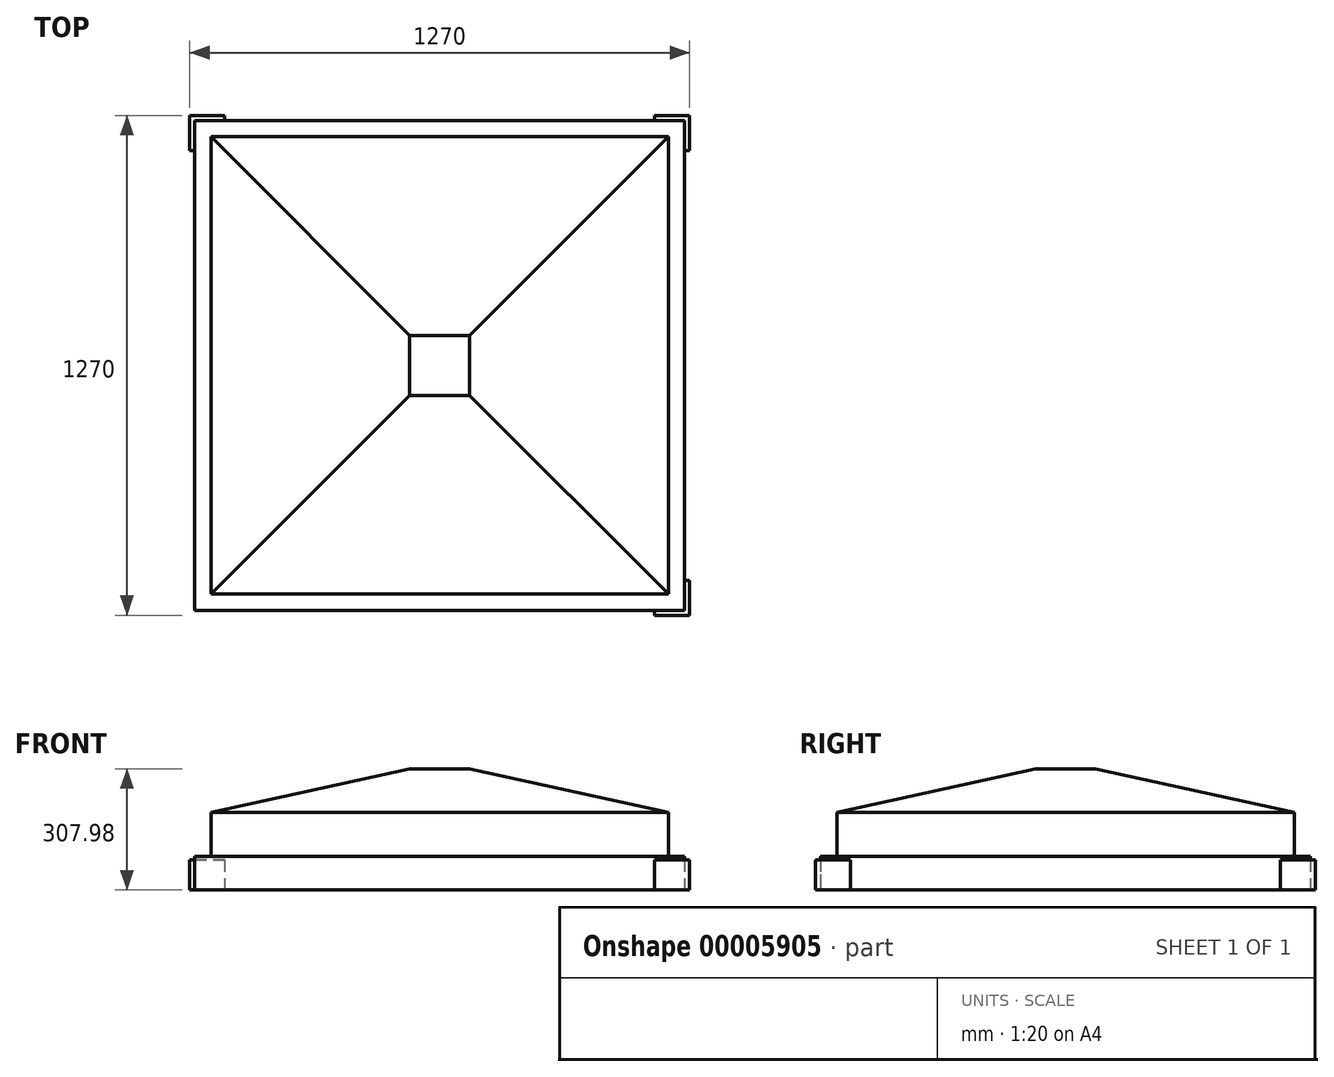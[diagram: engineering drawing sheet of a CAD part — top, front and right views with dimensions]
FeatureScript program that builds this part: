
annotation { "Feature Type Name" : "Feature", "Feature Type Description" : "" }
export const myFeature = defineFeature(function(context is Context, id is Id, definition is map)
    precondition{}
    {
        {
            var Q0;
            Q0=qCreatedBy(makeId("Top.planeOp"),FACE);
            var sketch = newSketch(context, id + "F0", { "sketchPlane" : qUnion([Q0])});
            skLineSegment(sketch, "E0.bottom", {"start": v(0, 0) * mm, "end": v(1244.6, 0) * mm});
            skLineSegment(sketch, "E0.top", {"start": v(0, 1244.6) * mm, "end": v(1244.6, 1244.6) * mm});
            skLineSegment(sketch, "E0.left", {"start": v(0, 0) * mm, "end": v(0, 1244.6) * mm});
            skLineSegment(sketch, "E0.right", {"start": v(1244.6, 0) * mm, "end": v(1244.6, 1244.6) * mm});
            skSolve(sketch);
        }
        {
            var Q0;
            Q0=makeQuery(id+"F0.imprint","IMPRINT",FACE,{"disambiguationData":[TD([[makeQuery(id+"F0.imprint","IMPRINT",EDGE,{"derivedFrom":sQuery(id+"F0.wireOp",EDGE,"E0.bottom")}),1.0]])]});
            extrude(context, id + "F1", {"entities" : qUnion([Q0]), "depth" : 85.72 * mm});
        }
        {
            var Q0;
            Q0=makeQuery(id+"F1.opExtrude","CAP_FACE",FACE,{"disambiguationData":[OSD([sQuery(id+"F0.wireOp",EDGE,"E0.bottom"),sQuery(id+"F0.wireOp",EDGE,"E0.top"),sQuery(id+"F0.wireOp",EDGE,"E0.left"),sQuery(id+"F0.wireOp",EDGE,"E0.right")])],"isStart":false});
            var sketch = newSketch(context, id + "F2", { "sketchPlane" : qUnion([Q0])});
            skLineSegment(sketch, "E1.bottom", {"start": v(41.28, 1203.33) * mm, "end": v(1203.33, 1203.33) * mm});
            skLineSegment(sketch, "E1.top", {"start": v(41.28, 41.28) * mm, "end": v(1203.33, 41.28) * mm});
            skLineSegment(sketch, "E1.left", {"start": v(41.27, 1203.33) * mm, "end": v(41.28, 41.28) * mm});
            skLineSegment(sketch, "E1.right", {"start": v(1203.33, 1203.33) * mm, "end": v(1203.33, 41.28) * mm});
            skLineSegment(sketch, "E2.0", {"start": v(0, 0) * mm, "end": v(0, 1244.6) * mm});
            skLineSegment(sketch, "E3.0", {"start": v(0, 1244.6) * mm, "end": v(1244.6, 1244.6) * mm});
            skLineSegment(sketch, "E4", {"start": v(0, 887.33) * mm, "end": v(41.28, 887.33) * mm, "construction": true});
            skLineSegment(sketch, "E5", {"start": v(395.74, 1244.6) * mm, "end": v(395.74, 1203.33) * mm, "construction": true});
            skSolve(sketch);
        }
        {
            var Q0;
            Q0=makeQuery(id+"F2.imprint","IMPRINT",FACE,{"disambiguationData":[TD([[makeQuery(id+"F2.imprint","IMPRINT",EDGE,{"derivedFrom":sQuery(id+"F2.wireOp",EDGE,"E1.bottom")}),-1.0]])]});
            extrude(context, id + "F3", {"entities" : qUnion([Q0]), "depth" : 111.12 * mm});
        }
        {
            var Q0;
            Q0=makeQuery(id+"F3.opExtrude","CAP_FACE",FACE,{"disambiguationData":[OSD([sQuery(id+"F2.wireOp",EDGE,"E1.bottom"),sQuery(id+"F2.wireOp",EDGE,"E1.top"),sQuery(id+"F2.wireOp",EDGE,"E1.left"),sQuery(id+"F2.wireOp",EDGE,"E1.right")])],"isStart":false});
            cPlane(context, id + "F4", {"entities" : qUnion([Q0]), "cplaneType" : CPlaneType.OFFSET, "offset" : 111.12 * mm, "width" : 152.4 * mm, "height" : 152.4 * mm});
        }
        {
            var Q0;
            Q0=qCreatedBy(id+"F4.planeOp",FACE);
            var sketch = newSketch(context, id + "F5", { "sketchPlane" : qUnion([Q0])});
            skLineSegment(sketch, "E6.0", {"start": v(41.27, 1203.33) * mm, "end": v(41.28, 41.28) * mm});
            skLineSegment(sketch, "E7.0", {"start": v(41.27, 1203.33) * mm, "end": v(1203.33, 1203.33) * mm});
            skLineSegment(sketch, "E8.bottom", {"start": v(546.1, 698.5) * mm, "end": v(698.5, 698.5) * mm});
            skLineSegment(sketch, "E8.top", {"start": v(546.1, 546.1) * mm, "end": v(698.5, 546.1) * mm});
            skLineSegment(sketch, "E8.left", {"start": v(546.1, 698.5) * mm, "end": v(546.1, 546.1) * mm});
            skLineSegment(sketch, "E8.right", {"start": v(698.5, 698.5) * mm, "end": v(698.5, 546.1) * mm});
            skLineSegment(sketch, "E9", {"start": v(546.1, 622.3) * mm, "end": v(41.28, 622.3) * mm, "construction": true});
            skLineSegment(sketch, "E10", {"start": v(622.3, 698.5) * mm, "end": v(622.3, 1203.33) * mm, "construction": true});
            skSolve(sketch);
        }
        {
            var Q0;
            Q0=makeQuery(id+"F3.opExtrude","CAP_FACE",FACE,{"disambiguationData":[OSD([sQuery(id+"F2.wireOp",EDGE,"E1.bottom"),sQuery(id+"F2.wireOp",EDGE,"E1.top"),sQuery(id+"F2.wireOp",EDGE,"E1.left"),sQuery(id+"F2.wireOp",EDGE,"E1.right")])],"isStart":false});
            var sketch = newSketch(context, id + "F6", { "sketchPlane" : qUnion([Q0])});
            skLineSegment(sketch, "E11.bottom", {"start": v(41.28, 41.28) * mm, "end": v(1203.33, 41.28) * mm});
            skLineSegment(sketch, "E11.top", {"start": v(41.28, 1203.33) * mm, "end": v(1203.33, 1203.33) * mm});
            skLineSegment(sketch, "E11.left", {"start": v(41.28, 41.28) * mm, "end": v(41.28, 1203.33) * mm});
            skLineSegment(sketch, "E11.right", {"start": v(1203.33, 41.28) * mm, "end": v(1203.33, 1203.33) * mm});
            skSolve(sketch);
        }
        {
            var Q0;
            Q0=makeQuery(id+"F6.imprint","IMPRINT",FACE,{"disambiguationData":[TD([[makeQuery(id+"F6.imprint","IMPRINT",EDGE,{"derivedFrom":sQuery(id+"F6.wireOp",EDGE,"E11.bottom")}),1.0]])]});
            var Q1;
            Q1=makeQuery(id+"F5.imprint","IMPRINT",FACE,{"disambiguationData":[TD([[makeQuery(id+"F5.imprint","IMPRINT",EDGE,{"derivedFrom":sQuery(id+"F5.wireOp",EDGE,"E8.bottom")}),-1.0]])]});
            loft(context, id + "F7", {"sheetProfilesArray" : [{ "sheetProfileEntities" : qUnion([Q0]) }, { "sheetProfileEntities" : qUnion([Q1]) }]});
        }
        {
            var Q0;
            Q0=makeQuery(id+"F1.opExtrude","CAP_FACE",FACE,{"disambiguationData":[OSD([sQuery(id+"F0.wireOp",EDGE,"E0.bottom"),sQuery(id+"F0.wireOp",EDGE,"E0.top"),sQuery(id+"F0.wireOp",EDGE,"E0.left"),sQuery(id+"F0.wireOp",EDGE,"E0.right")])],"isStart":false});
            var sketch = newSketch(context, id + "F8", { "sketchPlane" : qUnion([Q0])});
            skLineSegment(sketch, "E12.0", {"start": v(41.28, 41.28) * mm, "end": v(1203.33, 41.28) * mm});
            skLineSegment(sketch, "E13.0", {"start": v(1203.33, 1203.33) * mm, "end": v(1203.33, 41.28) * mm});
            skLineSegment(sketch, "E14.0", {"start": v(41.27, 1203.33) * mm, "end": v(1203.33, 1203.33) * mm});
            skLineSegment(sketch, "E15.0", {"start": v(41.27, 1203.33) * mm, "end": v(41.28, 41.28) * mm});
            skLineSegment(sketch, "E16", {"start": v(622.3, 1203.33) * mm, "end": v(622.3, 41.28) * mm, "construction": true});
            skLineSegment(sketch, "E17", {"start": v(41.28, 622.3) * mm, "end": v(1203.33, 622.3) * mm, "construction": true});
            skLineSegment(sketch, "E18", {"start": v(312.33, 1203.33) * mm, "end": v(312.33, 622.3) * mm, "construction": true});
            skLineSegment(sketch, "E19", {"start": v(41.28, 923.33) * mm, "end": v(622.3, 923.33) * mm, "construction": true});
            skSolve(sketch);
        }
        {
            var Q0;
            Q0=qCreatedBy(makeId("Top.planeOp"),FACE);
            var sketch = newSketch(context, id + "F9", { "sketchPlane" : qUnion([Q0])});
            skLineSegment(sketch, "E20.0", {"start": v(0, 0) * mm, "end": v(1244.6, 0) * mm});
            skLineSegment(sketch, "E21.0", {"start": v(0, 0) * mm, "end": v(0, 1244.6) * mm});
            skLineSegment(sketch, "E22.bottom", {"start": v(76.2, 0) * mm, "end": v(0, 0) * mm});
            skLineSegment(sketch, "E22.top", {"start": v(76.2, -12.7) * mm, "end": v(-12.7, -12.7) * mm});
            skLineSegment(sketch, "E22.left", {"start": v(76.2, 0) * mm, "end": v(76.2, -12.7) * mm});
            skLineSegment(sketch, "E22.right", {"start": v(-12.7, 0) * mm, "end": v(-12.7, -12.7) * mm});
            skLineSegment(sketch, "E23", {"start": v(-12.7, -6.35) * mm, "end": v(0, -6.35) * mm, "construction": true});
            skLineSegment(sketch, "E24.top", {"start": v(0, 76.2) * mm, "end": v(-12.7, 76.2) * mm});
            skLineSegment(sketch, "E24.left", {"start": v(0, 0) * mm, "end": v(0, 76.2) * mm});
            skLineSegment(sketch, "E24.right", {"start": v(-12.7, 0) * mm, "end": v(-12.7, 76.2) * mm});
            skLineSegment(sketch, "E25.0.MirrorCS", {"start": v(-12.7, 1244.6) * mm, "end": v(-12.7, 1168.4) * mm});
            skLineSegment(sketch, "E26.0.MirrorCS", {"start": v(76.2, 1257.3) * mm, "end": v(-12.7, 1257.3) * mm});
            skLineSegment(sketch, "E27.0.MirrorCS", {"start": v(76.2, 1244.6) * mm, "end": v(76.2, 1257.3) * mm});
            skLineSegment(sketch, "E28.0.MirrorCS", {"start": v(-12.7, 1244.6) * mm, "end": v(-12.7, 1257.3) * mm});
            skLineSegment(sketch, "E29", {"start": v(-12.7, 1168.4) * mm, "end": v(0, 1168.4) * mm});
            skLineSegment(sketch, "E30", {"start": v(0, 1168.4) * mm, "end": v(0, 1244.6) * mm});
            skLineSegment(sketch, "E31", {"start": v(0, 1244.6) * mm, "end": v(76.2, 1244.6) * mm});
            skLineSegment(sketch, "E32.0.MirrorCS", {"start": v(1168.4, 1257.3) * mm, "end": v(1257.3, 1257.3) * mm});
            skLineSegment(sketch, "E33.0.MirrorCS", {"start": v(1257.3, 1244.6) * mm, "end": v(1257.3, 1257.3) * mm});
            skLineSegment(sketch, "E34.0.MirrorCS", {"start": v(1257.3, 1244.6) * mm, "end": v(1257.3, 1168.4) * mm});
            skLineSegment(sketch, "E35.0.MirrorCS", {"start": v(1257.3, 1168.4) * mm, "end": v(1244.6, 1168.4) * mm});
            skLineSegment(sketch, "E36.0.MirrorCS", {"start": v(1244.6, 1168.4) * mm, "end": v(1244.6, 1244.6) * mm});
            skLineSegment(sketch, "E37.0.MirrorCS", {"start": v(1168.4, 1244.6) * mm, "end": v(1168.4, 1257.3) * mm});
            skLineSegment(sketch, "E38.0.MirrorCS", {"start": v(1244.6, 1244.6) * mm, "end": v(1168.4, 1244.6) * mm});
            skLineSegment(sketch, "E39.0.MirrorCS", {"start": v(1244.6, 76.2) * mm, "end": v(1257.3, 76.2) * mm});
            skLineSegment(sketch, "E40.0.MirrorCS", {"start": v(1257.3, 0) * mm, "end": v(1257.3, 76.2) * mm});
            skLineSegment(sketch, "E41.0.MirrorCS", {"start": v(1257.3, 0) * mm, "end": v(1257.3, -12.7) * mm});
            skLineSegment(sketch, "E42.0.MirrorCS", {"start": v(1168.4, -12.7) * mm, "end": v(1257.3, -12.7) * mm});
            skLineSegment(sketch, "E43.0.MirrorCS", {"start": v(1168.4, 0) * mm, "end": v(1168.4, -12.7) * mm});
            skLineSegment(sketch, "E44", {"start": v(1168.4, 0) * mm, "end": v(1244.6, 0) * mm});
            skLineSegment(sketch, "E45", {"start": v(1244.6, 76.2) * mm, "end": v(1244.6, 0) * mm});
            skSolve(sketch);
        }
        {
            var Q0;
            {Q0=qUnion([makeQuery(id+"F9.imprint","IMPRINT",FACE,{"disambiguationData":[TD([[makeQuery(id+"F9.imprint","IMPRINT",EDGE,{"derivedFrom":sQuery(id+"F9.wireOp",EDGE,"E22.bottom")}),1.0]])]}),makeQuery(id+"F9.imprint","IMPRINT",FACE,{"disambiguationData":[TD([[makeQuery(id+"F9.imprint","IMPRINT",EDGE,{"derivedFrom":sQuery(id+"F9.wireOp",EDGE,"E25.0.MirrorCS")}),1.0]])]}),makeQuery(id+"F9.imprint","IMPRINT",FACE,{"disambiguationData":[TD([[makeQuery(id+"F9.imprint","IMPRINT",EDGE,{"derivedFrom":sQuery(id+"F9.wireOp",EDGE,"E32.0.MirrorCS")}),-1.0]])]}),makeQuery(id+"F9.imprint","IMPRINT",FACE,{"disambiguationData":[TD([[makeQuery(id+"F9.imprint","IMPRINT",EDGE,{"derivedFrom":sQuery(id+"F9.wireOp",EDGE,"E39.0.MirrorCS")}),-1.0]])]})]);}
            extrude(context, id + "F10", {"entities" : qUnion([Q0]), "operationType" : NewBodyOperationType.ADD, "depth" : 76.2 * mm});
        }
    });
